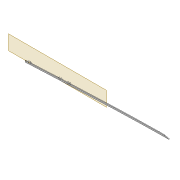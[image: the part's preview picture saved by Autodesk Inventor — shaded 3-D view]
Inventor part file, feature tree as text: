
AUTODESK INVENTOR PART (.ipt)
format: ipt  version: 2022 (Build 260153000, 153)  size: 548,864 bytes
history: native  units: mm
features: sketch x9, projected_geometry x9, extrude x8, fillet x2, shell x1, plane x1, chamfer x1
ambient origin geometry x8: Origin, YZ Plane, XZ Plane, XY Plane, X Axis, Y Axis, Z Axis, Center Point
bodies: Solid1 (feature_tree)
feature tree (31):
  extrude  "Extrusion1"  Depth=4.0mm
  shell  "Shell1"  Thickness=2.0mm
  extrude  "Extrusion8"  Depth=5.9mm
  extrude  "Extrusion3"  Depth=10.0mm TaperAngle=0.0deg
  extrude  "Extrusion4"  Depth=5.0mm
  fillet  "Fillet1"  Radius=5.0mm
  sketch  "Sketch10"  dims[d22=2.0mm d23=0.0mm d31=2.0mm d32=5.0mm]
  extrude  "Extrusion5"  Depth=2.5mm
  plane  "Work Plane2"
  extrude  "Extrusion9"  Depth=5.0mm
  fillet  "Fillet2"  Radius=2.5mm
  extrude  "Extrusion10"  Depth=6.0mm
  chamfer  "Chamfer1"  Distance=2.0mm
  extrude  "Extrusion12"  Depth=12.0mm
  sketch  "Sketch29"  dims[d66=3.0mm d67=12.0mm]
  sketch  "Sketch30"  dims[d68=5.0mm d69=15.0mm d70=12.0mm d71=3.05mm d72=10.0mm d73=0.0mm d74=2.0mm d75=100.0mm d76=20.0mm d77=0.5mm d78=10.0mm d79=0.0mm d82=3.0mm d83=2.0mm d84=45.0deg d85=1.0mm d86=1.0mm d87=1.0mm d88=1.0mm d89=1.0mm d91=1.0mm d92=10.0mm d93=0.0mm]
  sketch  "Sketch3"  dims[d0=2.0mm d1=0.0mm d2=4.0mm d7=2.0mm]
  sketch  "Sketch8"  dims[d8=2.0mm d9=5.9mm]
  sketch  "Sketch9"  dims[d13=10.0mm d14=0.0mm d16=10.0mm d17=0.0mm]
  projected_geometry  "Projected Loop4"
  projected_geometry  "Projected Loop10"
  sketch  "Sketch24"  dims[d34=1.6mm d35=2.5mm]
  projected_geometry  "Projected Loop11"
  projected_geometry  "Projected Loop12"
  projected_geometry  "Projected Loop13"
  sketch  "Sketch26"  dims[d37=5.0mm d38=1.6mm d40=2.5mm]
  projected_geometry  "Projected Loop14"
  sketch  "Sketch28"  dims[d62=80.0mm d63=6.0mm d64=2.0mm d65=0.0mm]
  projected_geometry  "Project Cut Edges1"
  projected_geometry  "Project Cut Edges2"
  projected_geometry  "Project Cut Edges3"
